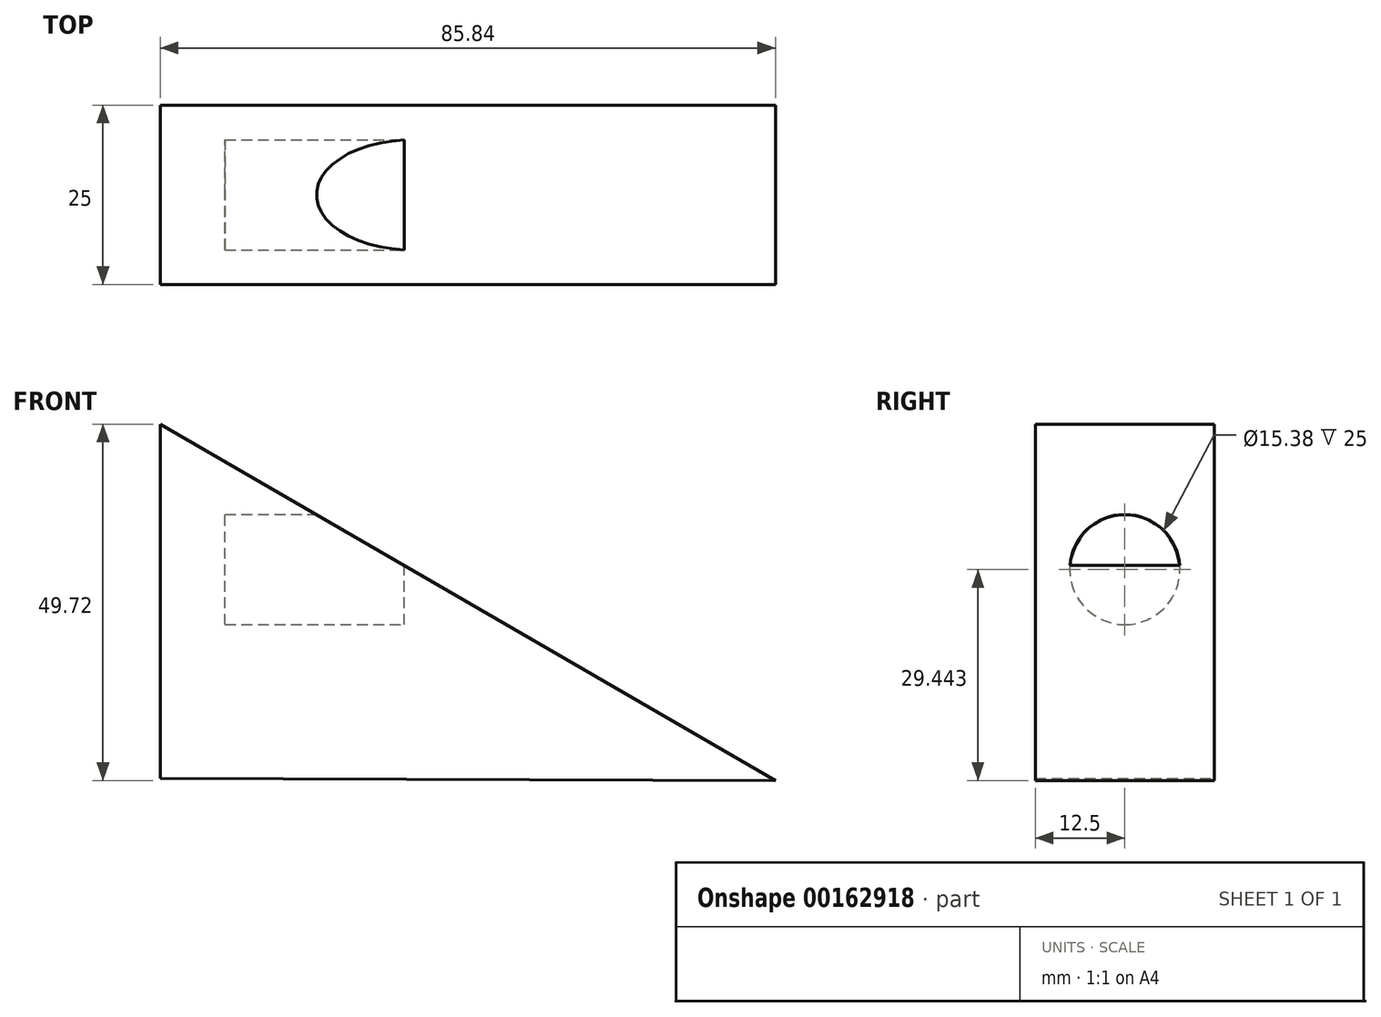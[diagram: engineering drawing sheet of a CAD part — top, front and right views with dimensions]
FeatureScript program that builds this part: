
annotation { "Feature Type Name" : "Feature", "Feature Type Description" : "" }
export const myFeature = defineFeature(function(context is Context, id is Id, definition is map)
    precondition{}
    {
        {
            var Q0;
            Q0=qCreatedBy(makeId("Front.planeOp"),FACE);
            var sketch = newSketch(context, id + "F0", { "sketchPlane" : qUnion([Q0])});
            skLineSegment(sketch, "E0", {"start": v(-34.03, 7.92) * mm, "end": v(-34.03, 57.36) * mm});
            skLineSegment(sketch, "E1", {"start": v(-34.03, 57.36) * mm, "end": v(51.8, 7.64) * mm});
            skLineSegment(sketch, "E2", {"start": v(51.8, 7.64) * mm, "end": v(-34.03, 7.92) * mm});
            skSolve(sketch);
        }
        {
            var Q0;
            Q0 = qSketchRegion(id + "F0", true);
            extrude(context, id + "F1", {"entities" : qUnion([Q0]), "depth" : 25 * mm, "symmetric" : true});
        }
        {
            var Q0;
            Q0=qCreatedBy(makeId("Right.planeOp"),FACE);
            var sketch = newSketch(context, id + "F2", { "sketchPlane" : qUnion([Q0])});
            skCircle(sketch, "E3", {"center": v(0, 37.08) * mm, "radius": 7.69 * mm});
            skSolve(sketch);
        }
        {
            var Q0;
            Q0 = qSketchRegion(id + "F2", true);
            extrude(context, id + "F3", {"entities" : qUnion([Q0]), "operationType" : NewBodyOperationType.REMOVE, "oppositeDirection" : true, "depth" : 25 * mm});
        }
    });
